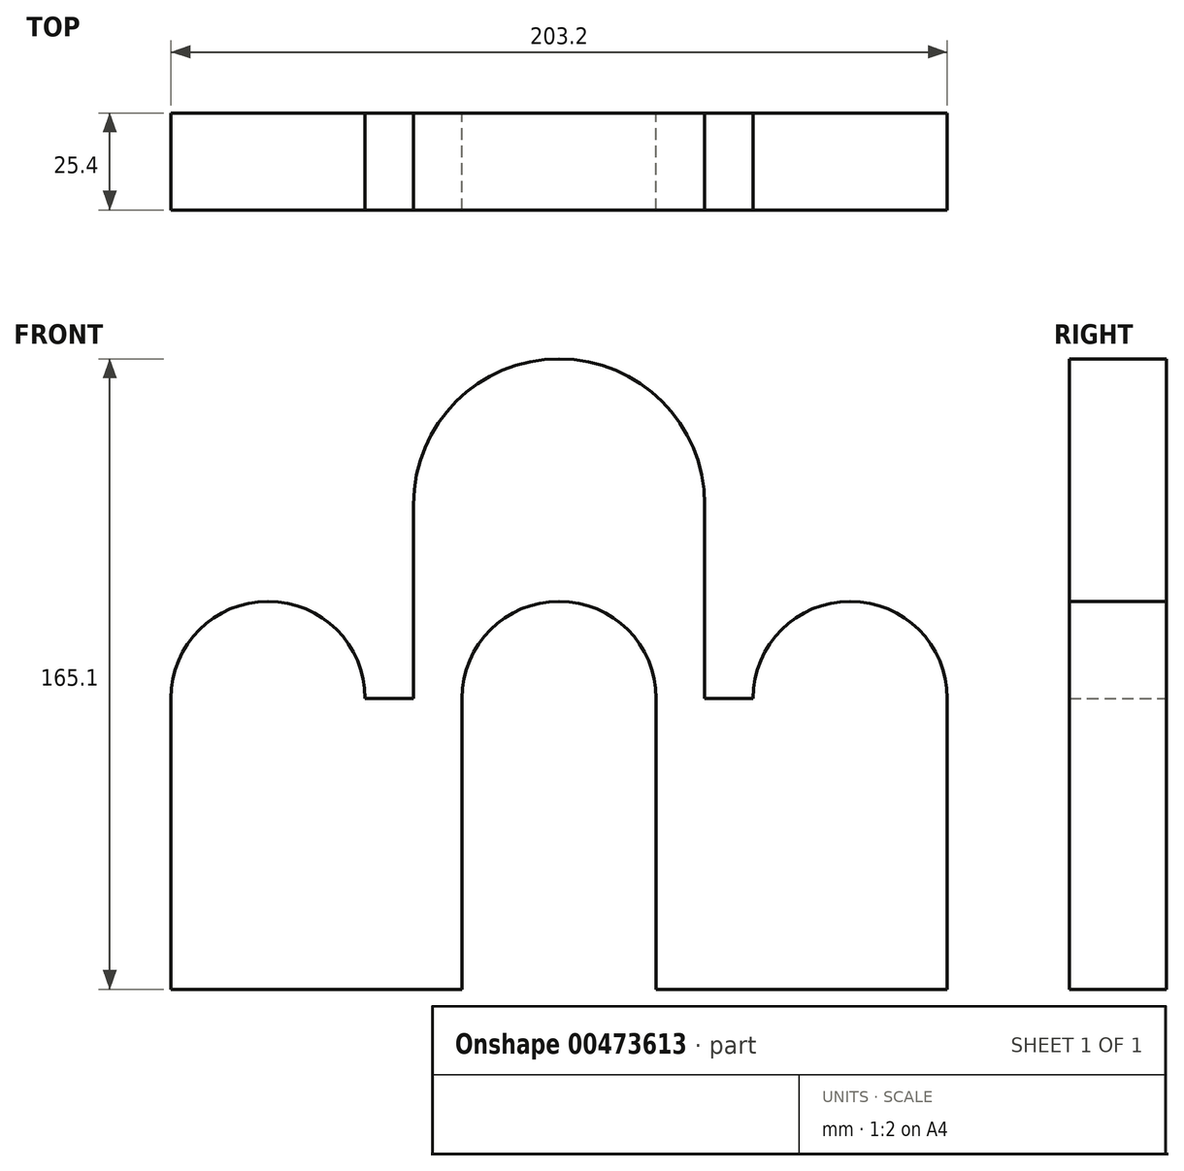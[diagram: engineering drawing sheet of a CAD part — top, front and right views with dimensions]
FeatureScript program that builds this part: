
annotation { "Feature Type Name" : "Feature", "Feature Type Description" : "" }
export const myFeature = defineFeature(function(context is Context, id is Id, definition is map)
    precondition{}
    {
        {
            var Q0;
            Q0=qCreatedBy(makeId("Front.planeOp"),FACE);
            var sketch = newSketch(context, id + "F0", { "sketchPlane" : qUnion([Q0])});
            skLineSegment(sketch, "E0", {"start": v(0, 0) * mm, "end": v(76.2, 0) * mm});
            skLineSegment(sketch, "E1", {"start": v(76.2, 0) * mm, "end": v(76.2, 76.2) * mm});
            skLineSegment(sketch, "E2", {"start": v(0, 0) * mm, "end": v(0, 76.2) * mm});
            skArc(sketch, "E3", {"start": v(0, 76.2) * mm, "mid": v(25.4, 101.6) * mm, "end": v(50.8, 76.2) * mm});
            skLineSegment(sketch, "E4", {"start": v(0, 76.2) * mm, "end": v(50.8, 76.2) * mm, "construction": true});
            skArc(sketch, "E5", {"start": v(76.2, 76.2) * mm, "mid": v(83.64, 94.16) * mm, "end": v(101.6, 101.6) * mm});
            skLineSegment(sketch, "E6", {"start": v(101.6, 76.2) * mm, "end": v(101.6, 127) * mm, "construction": true});
            skLineSegment(sketch, "E7", {"start": v(50.8, 76.2) * mm, "end": v(63.5, 76.2) * mm});
            skLineSegment(sketch, "E8", {"start": v(63.5, 76.2) * mm, "end": v(63.5, 127) * mm});
            skArc(sketch, "E9", {"start": v(63.5, 127) * mm, "mid": v(74.66, 153.94) * mm, "end": v(101.6, 165.1) * mm});
            skArc(sketch, "E10.MirrorCS", {"start": v(139.7, 127) * mm, "mid": v(128.54, 153.94) * mm, "end": v(101.6, 165.1) * mm});
            skLineSegment(sketch, "E11.MirrorCS", {"start": v(152.4, 76.2) * mm, "end": v(139.7, 76.2) * mm});
            skArc(sketch, "E12.MirrorCS", {"start": v(203.2, 76.2) * mm, "mid": v(177.8, 101.6) * mm, "end": v(152.4, 76.2) * mm});
            skLineSegment(sketch, "E13.MirrorCS", {"start": v(203.2, 0) * mm, "end": v(203.2, 76.2) * mm});
            skLineSegment(sketch, "E14.MirrorCS", {"start": v(203.2, 0) * mm, "end": v(127, 0) * mm});
            skLineSegment(sketch, "E15.MirrorCS", {"start": v(127, 0) * mm, "end": v(127, 76.2) * mm});
            skArc(sketch, "E16.MirrorCS", {"start": v(127, 76.2) * mm, "mid": v(119.56, 94.16) * mm, "end": v(101.6, 101.6) * mm});
            skLineSegment(sketch, "E17.MirrorCS", {"start": v(139.7, 76.2) * mm, "end": v(139.7, 127) * mm});
            skSolve(sketch);
        }
        {
            var Q0;
            Q0 = qSketchRegion(id + "F0", true);
            extrude(context, id + "F1", {"entities" : qUnion([Q0]), "depth" : 25.4 * mm});
        }
    });
